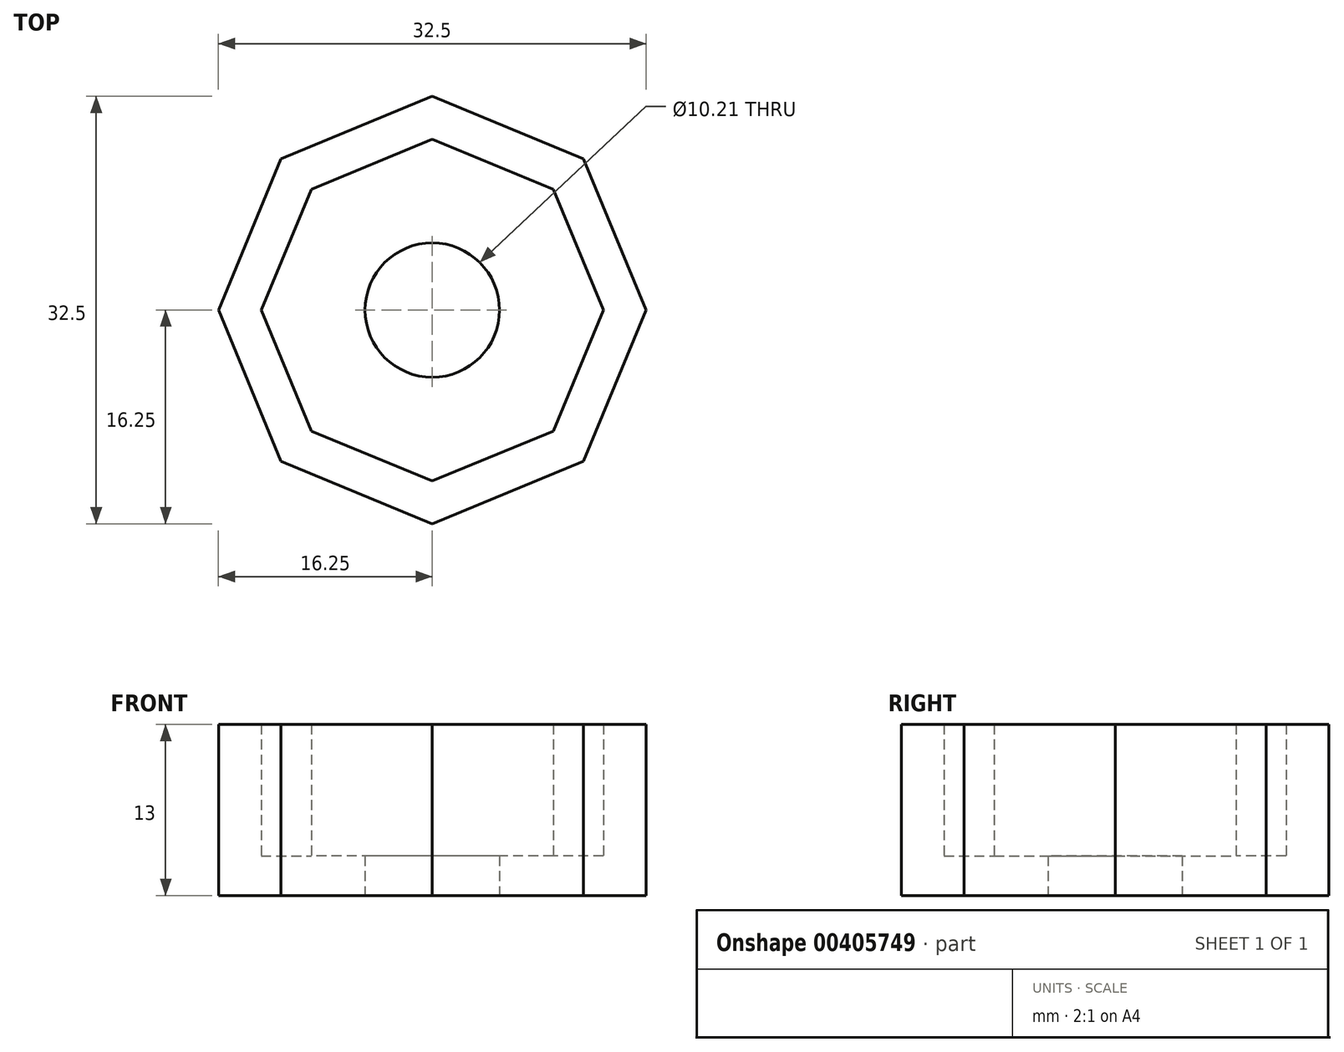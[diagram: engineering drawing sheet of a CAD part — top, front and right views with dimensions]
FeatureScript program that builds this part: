
annotation { "Feature Type Name" : "Feature", "Feature Type Description" : "" }
export const myFeature = defineFeature(function(context is Context, id is Id, definition is map)
    precondition{}
    {
        {
            var Q0;
            Q0=qCreatedBy(makeId("Top.planeOp"),FACE);
            var sketch = newSketch(context, id + "F0", { "sketchPlane" : qUnion([Q0])});
            skCircle(sketch, "E0.cCircle", {"center": v(0, 0) * mm, "radius": 12.01 * mm, "construction": true});
            skLineSegment(sketch, "E0.0", {"start": v(9.2, 9.2) * mm, "end": v(13, 0) * mm});
            skLineSegment(sketch, "E0.1", {"start": v(13, 0) * mm, "end": v(9.2, -9.2) * mm});
            skLineSegment(sketch, "E0.2", {"start": v(9.2, -9.2) * mm, "end": v(0, -13) * mm});
            skLineSegment(sketch, "E0.3", {"start": v(0, -13) * mm, "end": v(-9.2, -9.2) * mm});
            skLineSegment(sketch, "E0.4", {"start": v(-9.2, -9.2) * mm, "end": v(-13, 0) * mm});
            skLineSegment(sketch, "E0.5", {"start": v(-13, 0) * mm, "end": v(-9.2, 9.2) * mm});
            skLineSegment(sketch, "E0.6", {"start": v(-9.2, 9.2) * mm, "end": v(0, 13) * mm});
            skLineSegment(sketch, "E0.7", {"start": v(0, 13) * mm, "end": v(9.2, 9.2) * mm});
            skPoint(sketch, "E0.0.midPoint", {"position": v(11.1, 4.6) * mm});
            skCircle(sketch, "E1", {"center": v(0, 0) * mm, "radius": 5.1 * mm});
            skLineSegment(sketch, "E2", {"start": v(0, 13) * mm, "end": v(0, -13) * mm, "construction": true});
            skLineSegment(sketch, "E3.0", {"start": v(-11.49, 11.49) * mm, "end": v(0, 16.25) * mm});
            skLineSegment(sketch, "E3.1", {"start": v(-16.25, 0) * mm, "end": v(-11.49, 11.49) * mm});
            skLineSegment(sketch, "E3.2", {"start": v(0, 16.25) * mm, "end": v(11.49, 11.49) * mm});
            skLineSegment(sketch, "E3.3", {"start": v(-11.49, -11.49) * mm, "end": v(-16.25, 0) * mm});
            skLineSegment(sketch, "E3.4", {"start": v(11.49, 11.49) * mm, "end": v(16.25, 0) * mm});
            skLineSegment(sketch, "E3.5", {"start": v(16.25, 0) * mm, "end": v(11.49, -11.49) * mm});
            skLineSegment(sketch, "E3.6", {"start": v(11.49, -11.49) * mm, "end": v(0, -16.25) * mm});
            skLineSegment(sketch, "E3.7", {"start": v(0, -16.25) * mm, "end": v(-11.49, -11.49) * mm});
            skSolve(sketch);
        }
        {
            var Q0;
            Q0=qCreatedBy(makeId("Top.planeOp"),FACE);
            var sketch = newSketch(context, id + "F1", { "sketchPlane" : qUnion([Q0])});
            skLineSegment(sketch, "E4.0", {"start": v(-16.25, 0) * mm, "end": v(-11.49, 11.49) * mm});
            skLineSegment(sketch, "E4.1", {"start": v(-11.49, -11.49) * mm, "end": v(-16.25, 0) * mm});
            skLineSegment(sketch, "E4.2", {"start": v(-11.49, 11.49) * mm, "end": v(0, 16.25) * mm});
            skLineSegment(sketch, "E4.3", {"start": v(0, -16.25) * mm, "end": v(-11.49, -11.49) * mm});
            skLineSegment(sketch, "E4.4", {"start": v(0, 16.25) * mm, "end": v(11.49, 11.49) * mm});
            skLineSegment(sketch, "E4.5", {"start": v(11.49, 11.49) * mm, "end": v(16.25, 0) * mm});
            skLineSegment(sketch, "E4.6", {"start": v(16.25, 0) * mm, "end": v(11.49, -11.49) * mm});
            skLineSegment(sketch, "E4.7", {"start": v(11.49, -11.49) * mm, "end": v(0, -16.25) * mm});
            skSolve(sketch);
        }
        {
            var Q0;
            Q0 = qSketchRegion(id + "F1", true);
            extrude(context, id + "F2", {"entities" : qUnion([Q0]), "depth" : 13 * mm});
        }
        {
            var Q0;
            Q0=makeQuery(id+"F2.opExtrude","CAP_FACE",FACE,{"disambiguationData":[OSD([sQuery(id+"F1.wireOp",EDGE,"E4.0"),sQuery(id+"F1.wireOp",EDGE,"E4.1"),sQuery(id+"F1.wireOp",EDGE,"E4.2"),sQuery(id+"F1.wireOp",EDGE,"E4.3"),sQuery(id+"F1.wireOp",EDGE,"E4.4"),sQuery(id+"F1.wireOp",EDGE,"E4.5"),sQuery(id+"F1.wireOp",EDGE,"E4.6"),sQuery(id+"F1.wireOp",EDGE,"E4.7")])],"isStart":false});
            shell(context, id + "F3", {"entities" : qUnion([Q0]), "thickness" : 3 * mm});
        }
        {
            var Q0;
            Q0=qCreatedBy(makeId("Top.planeOp"),FACE);
            var sketch = newSketch(context, id + "F4", { "sketchPlane" : qUnion([Q0])});
            skCircle(sketch, "E5.0", {"center": v(0, 0) * mm, "radius": 5.1 * mm});
            skSolve(sketch);
        }
        {
            var Q0;
            Q0 = qSketchRegion(id + "F4", true);
            extrude(context, id + "F5", {"entities" : qUnion([Q0]), "operationType" : NewBodyOperationType.REMOVE, "depth" : 25 * mm});
        }
    });
